# Revit family: puhv-hp224_280dmj_60Hz______
name_source: partatom
category: 機械設備
units: mm (PartAtom-declared; Revit-internal decimal feet)

## family parameters
OmniClass タイトル = Split System Air Conditioning Units
OmniClass 番号 = 23.75.10.24.21.27.27
パーツ タイプ = 標準
ロード時にボイドで切り取り = いいえ
丸型コネクタ寸法 = 直径を使用
作業面ベース = いいえ
共有 = いいえ
常に垂直 = はい
部屋計算ポイント = いいえ

## types (2) — shared parameters
Clearance Back = 300
Clearance Front = 450  [stored 1.47638 ft]
Clearance Left = 15  [stored 0.0492126 ft]
Clearance Right = 15  [stored 0.0492126 ft]
Clearance Top = 1000  [stored 3.28084 ft]
Depth = 740  [stored 2.42782 ft]
Height = 1650  [stored 5.41339 ft]
IfcExportAs = IfcUnitaryEquipmentType
IfcExportType = AIRCONDITIONINGUNIT
OmniClassCode = 23-33 17 13 11
URL = https://www.mitsubishielectric.co.jp
Uniclass2015Code = Pr_70_65_03_84
Uniclass2015Title = Split coil remote air cooled condensing units
Uniclass2015Version = Systems v1.9
Width = 920  [stored 3.01837 ft]
サービススペース = はい
サービススペース_タイプA = はい
ダクト下位置 = 89  [stored 0.291995 ft]
ダクト左位置 = 222
ダクト幅 = 140 mm
ダクト高 = 77 mm
ドレン管径 = 0.00 mm
仕様書バージョン = Version1.0
企業コード = 108420
冷媒ガス奥行き = 146  [stored 0.479003 ft]
冷媒ガス幅 = 83  [stored 0.27231 ft]
冷媒ガス高さ = 172  [stored 0.564304 ft]
冷媒液奥行き = 146  [stored 0.479003 ft]
冷媒液幅 = 251  [stored 0.823491 ft]
冷媒液管径 = 12.70 mm
冷媒液高さ = 222
冷媒管径 = 100.00 mm
分類コード = 50053003126100
参照している仕様書等のバージョン = 公共建築工事標準仕様書（機械設備工事編）平成31年度版
周波数 = 60 Hz
呼称 = パッケージ形空気調和機_室外機
始動方式 = 直入
形式 = パッケージ形 室外機
最小電線太さ_mm2 = 14
本体マテリアル = <カテゴリ別>
極数 = 3
法定耐用年数 = 15
発停方法 = 付属スイッチ
相 = 3
積算_科目 = 1 空気調和設備
符号 = PAC
製品リリース年月 = 2018年10月10日
製品出荷対象 = 国内
製造元 = 三菱電機株式会社
設置方法 = 床置形
説明 = 設備用パッケージエアコン 空冷床置形・冷暖兼用 ズバ暖ファシレアＤＤ
負荷分類 = 1_熱源類
運転方法 = 冷暖切替
運転質量 = 0.00 kg
電圧 = 200 V
電源幅 = 201  [stored 0.659449 ft]
電源径 = 65  [stored 0.213255 ft]
電源高さ = 217  [stored 0.711942 ft]
zero-valued in all types: APF, COP, 価格, 機械基礎_D, 機械基礎_H, 機械基礎_W

## per-type parameters (varying)
| type | 冷媒ガス管径 | 冷媒管径符号 | 冷房能力 | 形名 | 推奨ブレーカー容量 | 暖房能力 | 最大電流値 | 消費電力 | 消費電力_冷房 | 消費電力_暖房 | 製品質量 | 質量 | 電動機出力_圧縮機 | 電動機出力_送風機 | 音響パワーレベル(dB) |
| PUHV-HP224DMJ | 19.05 mm | Ce | 20 kW | PUHV-HP-DMJ : PUHV-HP224DMJ1 | 60 A | 22 kW | 48 A | 6230 W | 6230 W | 6120 W | 196.00 kg | 235.20 kg | 5390 W | 350 W | 80 |
| PUHV-HP280DMJ | 22.20 mm | Cf | 25 kW | PUHV-HP-DMJ : PUHV-HP280DMJ1 | 75 A | 28 kW | 59 A | 7500 W | 7500 W | 7300 W | 205.00 kg | 246.00 kg | 6180 W | 460 W | 83.5 |

note: column(s) folded — value = type name in every type: モデル

note: [stored X ft] marks values corroborated as IEEE doubles in the binary element streams (Revit-internal decimal feet)

## geometry (parser evidence)
native form markers: Blend x2
no freeform markers — native parametric forms only
